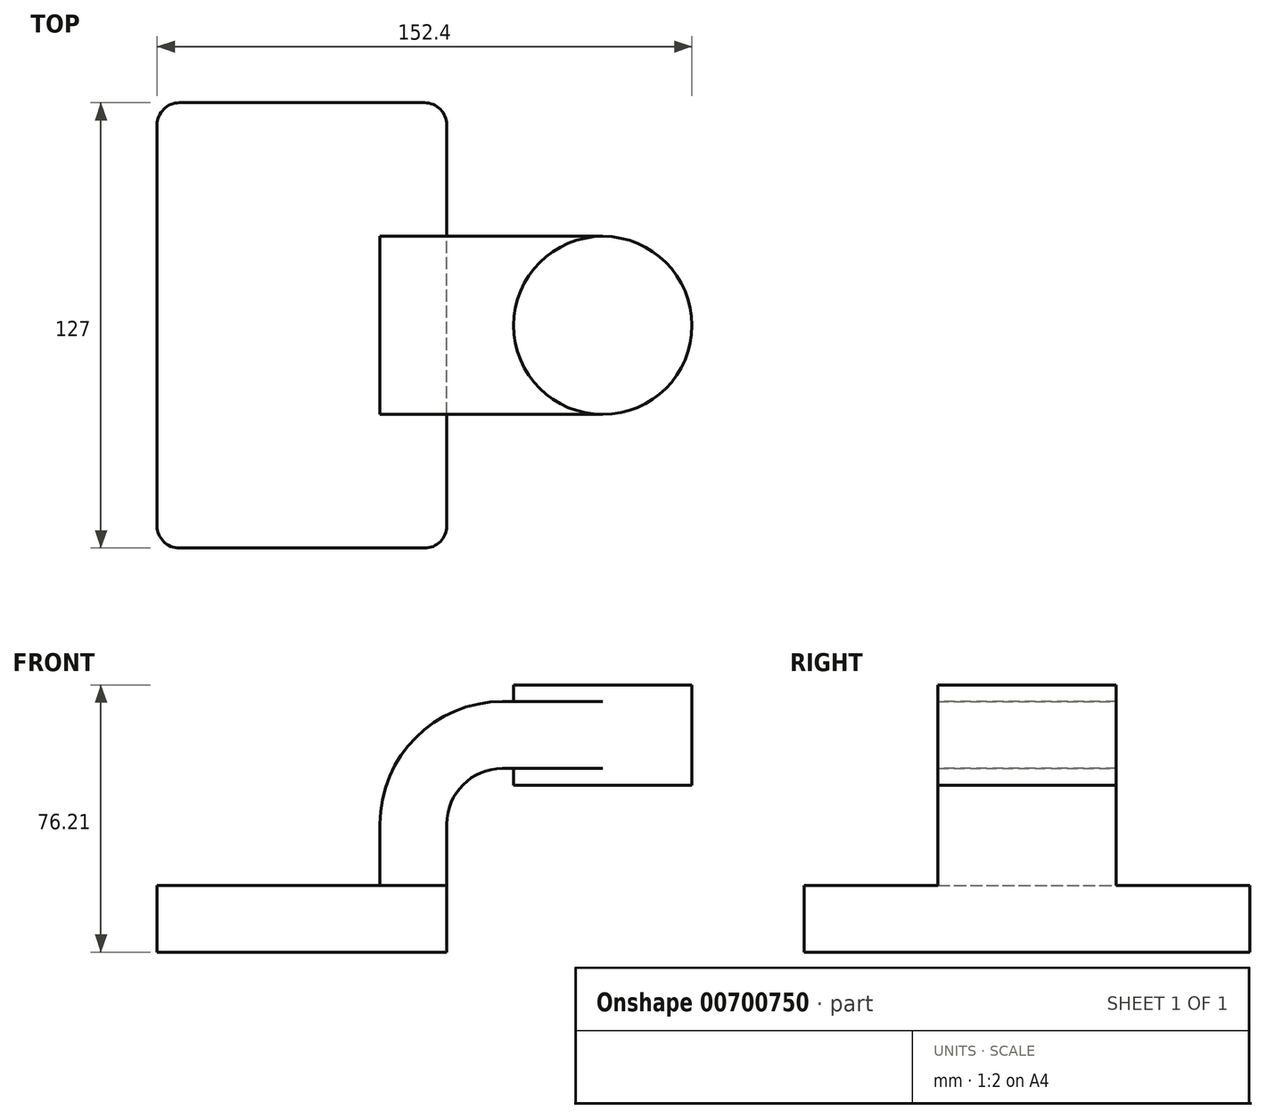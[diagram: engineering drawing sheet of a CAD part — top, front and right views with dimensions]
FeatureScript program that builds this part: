
annotation { "Feature Type Name" : "Feature", "Feature Type Description" : "" }
export const myFeature = defineFeature(function(context is Context, id is Id, definition is map)
    precondition{}
    {
        {
            var Q0;
            Q0=qCreatedBy(makeId("Front.planeOp"),FACE);
            var sketch = newSketch(context, id + "F0", { "sketchPlane" : qUnion([Q0])});
            skLineSegment(sketch, "E0.bottom", {"start": v(41.28, -9.53) * mm, "end": v(-41.28, -9.53) * mm});
            skLineSegment(sketch, "E0.top", {"start": v(41.28, 9.53) * mm, "end": v(-41.28, 9.53) * mm});
            skLineSegment(sketch, "E0.left", {"start": v(41.28, -9.52) * mm, "end": v(41.28, 9.53) * mm});
            skLineSegment(sketch, "E0.right", {"start": v(-41.28, -9.53) * mm, "end": v(-41.28, 9.52) * mm});
            skPoint(sketch, "E0.middle", {"position": v(0, 0) * mm});
            skLineSegment(sketch, "E1.bottom", {"start": v(111.12, 38.1) * mm, "end": v(60.33, 38.1) * mm});
            skLineSegment(sketch, "E1.top", {"start": v(111.12, 66.67) * mm, "end": v(60.33, 66.67) * mm});
            skLineSegment(sketch, "E1.left", {"start": v(111.13, 38.1) * mm, "end": v(111.13, 66.68) * mm});
            skLineSegment(sketch, "E1.right", {"start": v(60.33, 38.1) * mm, "end": v(60.33, 66.67) * mm});
            skPoint(sketch, "E1.middle", {"position": v(85.73, 52.39) * mm});
            skLineSegment(sketch, "E2", {"start": v(41.28, 9.53) * mm, "end": v(41.28, 26.99) * mm});
            skArc(sketch, "E3", {"start": v(41.28, 26.99) * mm, "mid": v(45.92, 38.21) * mm, "end": v(57.15, 42.86) * mm});
            skLineSegment(sketch, "E4", {"start": v(57.15, 42.86) * mm, "end": v(85.72, 42.86) * mm});
            skLineSegment(sketch, "E5.0", {"start": v(57.15, 61.91) * mm, "end": v(85.72, 61.91) * mm});
            skArc(sketch, "E5.1", {"start": v(22.23, 26.99) * mm, "mid": v(32.45, 51.68) * mm, "end": v(57.15, 61.91) * mm});
            skLineSegment(sketch, "E5.2", {"start": v(22.23, 9.53) * mm, "end": v(22.23, 26.99) * mm});
            skLineSegment(sketch, "E6", {"start": v(85.73, 66.67) * mm, "end": v(85.73, 38.1) * mm});
            skFitSpline(sketch, "E7", {"points": [v(-41.28, 9.53) * mm, v(57.15, 61.91) * mm], "startDerivative": vector(0, 87.97) * mm, "endDerivative": vector(126.38, 0) * mm});
            skSolve(sketch);
        }
        {
            var Q0;
            Q0=makeQuery(id+"F0.imprint","IMPRINT",FACE,{"disambiguationData":[TD([[makeQuery(id+"F0.imprint","IMPRINT",EDGE,{"derivedFrom":sQuery(id+"F0.wireOp",EDGE,"E0.bottom")}),-1.0]])]});
            extrude(context, id + "F1", {"entities" : qUnion([Q0]), "endBound" : BoundingType.SYMMETRIC, "depth" : 127 * mm, "offsetDistance" : 25.4 * mm});
        }
        {
            var Q0;
            {var subQ1=sQuery(id+"F0.wireOp",EDGE,"E2");Q0=makeQuery(id+"F0.imprint","IMPRINT",FACE,{"disambiguationData":[TD([[makeQuery(id+"F0.imprint","IMPRINT",EDGE,{"derivedFrom":subQ1}),1.0]])]});}
            var Q1;
            {var subQ0=sQuery(id+"F0.wireOp",EDGE,"E4");var subQ1=sQuery(id+"F0.wireOp",EDGE,"E1.right");var subQ2=makeQuery(id+"F0.imprint","INTERSECT",VERTEX,{"derivedFrom":[subQ1,subQ0]});Q1=makeQuery(id+"F0.imprint","IMPRINT",FACE,{"disambiguationData":[TD([[makeQuery(id+"F0.imprint","IMPRINT",EDGE,{"disambiguationData":[TD([[subQ2,-1.0]])],"derivedFrom":subQ1}),-1.0]])]});}
            extrude(context, id + "F2", {"entities" : qUnion([Q0, Q1]), "operationType" : NewBodyOperationType.ADD, "endBound" : BoundingType.SYMMETRIC, "depth" : 50.8 * mm, "offsetDistance" : 25.4 * mm});
        }
        {
            var Q0;
            Q0=makeQuery(id+"F0.imprint","IMPRINT",FACE,{"disambiguationData":[TD([[makeQuery(id+"F0.imprint","IMPRINT",EDGE,{"derivedFrom":sQuery(id+"F0.wireOp",EDGE,"E5.1")}),1.0]])]});
            extrude(context, id + "F3", {"entities" : qUnion([Q0]), "operationType" : NewBodyOperationType.ADD, "endBound" : BoundingType.SYMMETRIC, "depth" : 15.88 * mm, "offsetDistance" : 25.4 * mm});
        }
        {
            var Q0;
            {var subQ4=sQuery(id+"F0.wireOp",EDGE,"E1.left");Q0=makeQuery(id+"F0.imprint","IMPRINT",FACE,{"disambiguationData":[TD([[makeQuery(id+"F0.imprint","IMPRINT",EDGE,{"derivedFrom":subQ4}),1.0]])]});}
            var Q1;
            Q1=sQuery(id+"F0.wireOp",EDGE,"E6");
            revolve(context, id + "F4", {"operationType" : NewBodyOperationType.ADD, "entities" : qUnion([Q0]), "axis" : qUnion([Q1]), "revolveType" : RevolveType.FULL});
        }
        {
            var Q0;
            Q0=makeQuery(id+"F1.opExtrude","CAP_EDGE",EDGE,{"disambiguationData":[OSD([sQuery(id+"F0.wireOp",EDGE,"E0.left")])],"isStart":false});
            var Q1;
            Q1=makeQuery(id+"F1.opExtrude","CAP_EDGE",EDGE,{"disambiguationData":[OSD([sQuery(id+"F0.wireOp",EDGE,"E0.right")])],"isStart":false});
            var Q2;
            Q2=makeQuery(id+"F1.opExtrude","CAP_EDGE",EDGE,{"disambiguationData":[OSD([sQuery(id+"F0.wireOp",EDGE,"E0.left")])],"isStart":true});
            var Q3;
            Q3=makeQuery(id+"F1.opExtrude","CAP_EDGE",EDGE,{"disambiguationData":[OSD([sQuery(id+"F0.wireOp",EDGE,"E0.right")])],"isStart":true});
            fillet(context, id + "F5", {"entities" : qUnion([Q0, Q1, Q2, Q3]), "radius" : 6.35 * mm, "tangentPropagation" : true, "allowEdgeOverflow" : false});
        }
    });
